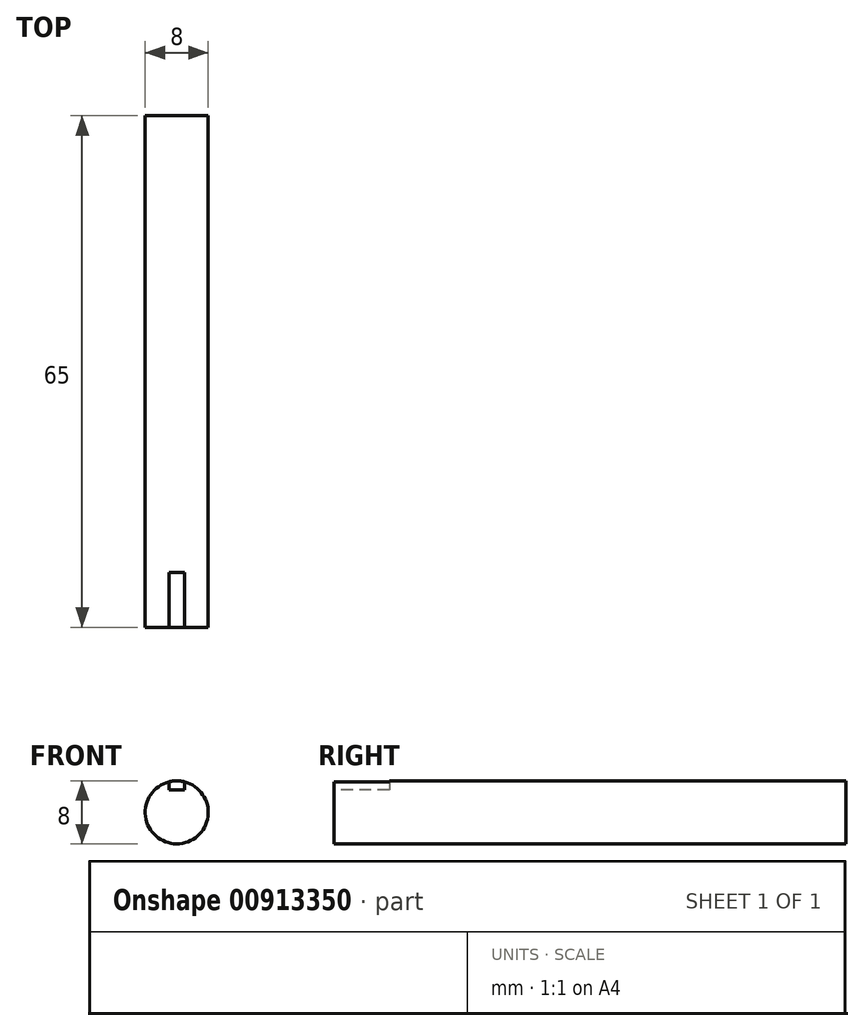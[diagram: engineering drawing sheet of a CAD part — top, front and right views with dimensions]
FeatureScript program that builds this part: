
annotation { "Feature Type Name" : "Feature", "Feature Type Description" : "" }
export const myFeature = defineFeature(function(context is Context, id is Id, definition is map)
    precondition{}
    {
        {
            var Q0;
            Q0=qCreatedBy(makeId("Front.planeOp"),FACE);
            var sketch = newSketch(context, id + "F0", { "sketchPlane" : qUnion([Q0])});
            skCircle(sketch, "E0", {"center": v(0, 0) * mm, "radius": 4 * mm});
            skSolve(sketch);
        }
        {
            var Q0;
            Q0 = qSketchRegion(id + "F0", true);
            extrude(context, id + "F1", {"entities" : qUnion([Q0]), "depth" : 65 * mm, "offsetDistance" : 25 * mm, "symmetric" : true});
        }
        {
            var Q0;
            Q0=makeQuery(id+"F1.opExtrude","CAP_FACE",FACE,{"disambiguationData":[OSD([sQuery(id+"F0.wireOp",EDGE,"E0")])],"isStart":false});
            var sketch = newSketch(context, id + "F2", { "sketchPlane" : qUnion([Q0])});
            skLineSegment(sketch, "E1", {"start": v(-1, 3.87) * mm, "end": v(-1, 2.87) * mm});
            skLineSegment(sketch, "E2", {"start": v(-1, 2.87) * mm, "end": v(1, 2.87) * mm});
            skLineSegment(sketch, "E3", {"start": v(1, 2.87) * mm, "end": v(1, 3.87) * mm});
            skLineSegment(sketch, "E4", {"start": v(1, 3.87) * mm, "end": v(0, 4.63) * mm});
            skLineSegment(sketch, "E5", {"start": v(0, 4.63) * mm, "end": v(-1, 3.87) * mm});
            skSolve(sketch);
        }
        {
            var Q0;
            Q0 = qSketchRegion(id + "F2", true);
            extrude(context, id + "F3", {"entities" : qUnion([Q0]), "operationType" : NewBodyOperationType.REMOVE, "oppositeDirection" : true, "depth" : 7 * mm, "offsetDistance" : 25 * mm});
        }
    });
